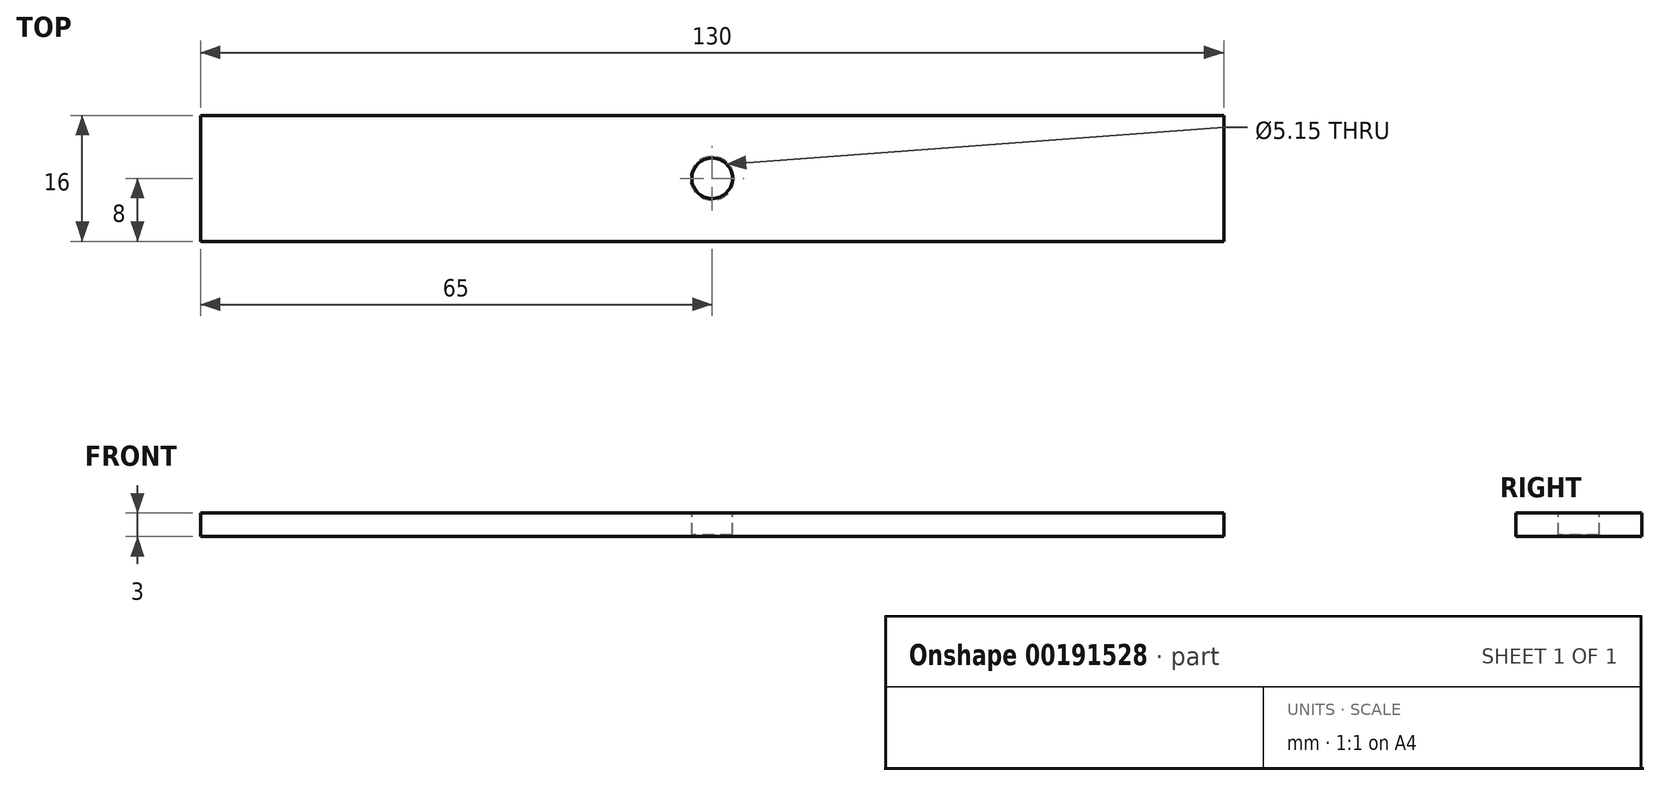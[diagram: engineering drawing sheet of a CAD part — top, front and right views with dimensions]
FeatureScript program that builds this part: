
annotation { "Feature Type Name" : "Feature", "Feature Type Description" : "" }
export const myFeature = defineFeature(function(context is Context, id is Id, definition is map)
    precondition{}
    {
        {
            var Q0;
            Q0=qCreatedBy(makeId("Top.planeOp"),FACE);
            var sketch = newSketch(context, id + "F0", { "sketchPlane" : qUnion([Q0])});
            skLineSegment(sketch, "E0.bottom", {"start": v(65, -8) * mm, "end": v(-65, -8) * mm});
            skLineSegment(sketch, "E0.top", {"start": v(65, 8) * mm, "end": v(-65, 8) * mm});
            skLineSegment(sketch, "E0.left", {"start": v(65, -8) * mm, "end": v(65, 8) * mm});
            skLineSegment(sketch, "E0.right", {"start": v(-65, -8) * mm, "end": v(-65, 8) * mm});
            skPoint(sketch, "E0.middle", {"position": v(0, 0) * mm});
            skSolve(sketch);
        }
        {
            var Q0;
            Q0 = qSketchRegion(id + "F0", true);
            extrude(context, id + "F1", {"entities" : qUnion([Q0]), "depth" : 3 * mm});
        }
        {
            var Q0;
            Q0=makeQuery(id+"F1.opExtrude","CAP_FACE",FACE,{"disambiguationData":[OSD([sQuery(id+"F0.wireOp",EDGE,"E0.bottom"),sQuery(id+"F0.wireOp",EDGE,"E0.top"),sQuery(id+"F0.wireOp",EDGE,"E0.left"),sQuery(id+"F0.wireOp",EDGE,"E0.right")])],"isStart":false});
            var sketch = newSketch(context, id + "F2", { "sketchPlane" : qUnion([Q0])});
            skCircle(sketch, "E1", {"center": v(0, 0) * mm, "radius": 2.58 * mm});
            skSolve(sketch);
        }
        {
            var Q0;
            Q0 = qSketchRegion(id + "F2", true);
            extrude(context, id + "F3", {"entities" : qUnion([Q0]), "operationType" : NewBodyOperationType.REMOVE, "endBound" : BoundingType.THROUGH_ALL, "oppositeDirection" : true, "depth" : 25 * mm});
        }
        {
            var Q0;
            Q0=makeQuery(id+"F3.boolean.opBoolean","COPY",EDGE,{"derivedFrom":makeQuery(id+"F3.opExtrude","CAP_EDGE",EDGE,{"disambiguationData":[OSD([sQuery(id+"F2.wireOp",EDGE,"E1")])],"isStart":true})});
            var Q1;
            Q1=makeQuery(id+"F3.boolean.opBoolean","INTERSECT",EDGE,{"derivedFrom":[makeQuery(id+"F1.opExtrude","CAP_FACE",FACE,{"disambiguationData":[OSD([sQuery(id+"F0.wireOp",EDGE,"E0.bottom"),sQuery(id+"F0.wireOp",EDGE,"E0.top"),sQuery(id+"F0.wireOp",EDGE,"E0.left"),sQuery(id+"F0.wireOp",EDGE,"E0.right")])],"isStart":true}),makeQuery(id+"F3.opExtrude","SWEPT_FACE",FACE,{"disambiguationData":[OSD([sQuery(id+"F2.wireOp",EDGE,"E1")])]})]});
            chamfer(context, id + "F4", {"entities" : qUnion([Q0, Q1]), "width" : .2 * mm, "tangentPropagation" : true});
        }
    });
